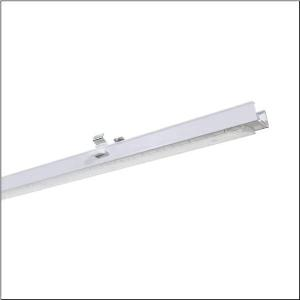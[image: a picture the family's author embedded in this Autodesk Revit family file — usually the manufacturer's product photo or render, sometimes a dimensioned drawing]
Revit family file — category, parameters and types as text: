
# Revit family: trunking_flex_31_51re12db49b
name_source: partatom
category: Lighting Fixtures
units: mm (PartAtom-declared; Revit-internal decimal feet)

## family parameters
Cut with Voids When Loaded = No
Host = Face
Light Source = No
Part Type = Normal
Room Calculation Point = No
Round Connector Dimension = Use Diameter
Shared = No

## types (1)
- --- (1 x LED, 8900 lm, 56 W, 4000K)
    Apparent Load = 56 VA
    CIE Flux Codes = 65 91 98 99 100
    Color Rendering = 80
    Color Temperature = 4000K
    Default Elevation = 1800 mm
    Description = Trunking Flex 31, luminaire insert, of extruded aluminium section, coated, traffic white (RAL 9016), length: 1.472mm, width: 91mm, height: 53mm, LED rated luminous flux: 8.900lm, light colour: 840, control gear: DALI 2, with system connector: socket, mains connection: 220..240V, AC, 50/60Hz, rated input power: 56W, primary light control with lens, of plastic, primary optical cover: cover, of PMMA, light emission: direct distribution, protection rating (complete): IP20, insulation class (complete): insulation class I (protective earthing), certification: CE, UKCA, impact resistance: IK02, permissible ambient temperature for indoor applications: -20..+40°C, packaging unit: 1 piece
    Height = 58 mm
    Lamp = 1 x LED
    Lamp Light Flux = 8900 lm
    Lamp Power = 56 W
    Lamp count = 1
    Length = 1472 mm
    Luminous efficacy = 159 lm/W
    Manufacturer = Siteco
    ModVariant = No
    Model = 51RE12DB49B
    Mounting Place = Ceiling
    Mounting Type = Pendant
    Number of Poles = 1
    OnlyDefault = Yes
    Power Factor = 1
    Product Name = Trunking Flex 31
    Product group = luminaire insert
    ProductGroupID = 901
    Protection Class = Protection class I
    Protection Degree = IP 20
    RLX_Detail_Level = 1
    RLX_Emergency_Light_Flux = 0 lm
    RLX_Emergency_Type = 0
    RLX_Emergency_Type_DB = No
    RlxData = <blob elided: 21769 chars, md5=919b1a30>
    Socket = socket
    Standby Power = 0 W
    System Light Flux = 8900 lm
    System Power = 56 W
    Type Comments = individual setting: luminous flux: 100 % | (OFF | ON | OFF | OFF) | 1200 mA
    Type Image = l_1266702.jpg
    URL = http://relux.com
    VarID = @adj_001315
    Voltage = 0 V
    Weight = 0.00 kg
    Width = 65 mm

## geometry (parser evidence)
native form markers: Blend x4, Sweep x12
no freeform markers — native parametric forms only
